FCSTD DOCUMENT  (FreeCAD 1.0RUnknown)
Label: mastersheet
License: All rights reserved
LicenseURL: https://en.wikipedia.org/wiki/All_rights_reserved
objects: Spreadsheet::Sheet×1

FEATURE [Spreadsheet::Sheet] Spreadsheet
  cells = A1='corpus_width; B1(corpus_width)=540; A2='corpus_depth; B2(corpus_depth)=600; A3='corpus_outer_thickness; B3(corpus_outer_thickness)=19; A4='corpus_backplate_thickness; B4(corpus_backplate_thickness)=9; A5='corpus_heigth; B5(corpus_height)=2045; A6='corpus01_heigth; B6(corpus01_height)=1415; A7='corpus02_heigth; B7(corpus02_height)=780; A8='drawer_outer_thickness; B8(drawer_outer_thickness)=19; A9='drawer_bottom_thickness; B9(drawer_bottom_thickness)=9; A10='drawer_length; B10(drawer_length)==B2 - 50; A11='drawer_width; B11(drawer_width)==B1 - 2 * 12.5 - 2 * B3; A12='drawer_bottom_tol; B12(drawer_bottom_tol)=0.5; A13='drawer_height; B13(drawer_height)=170; A14='drawer_slot_depth; B14(drawer_slot_depth)=8; A15='drawer_slot_height; B15(drawer_slot_height)=10; A16='hettich_height; B16(hettich_height)=30
